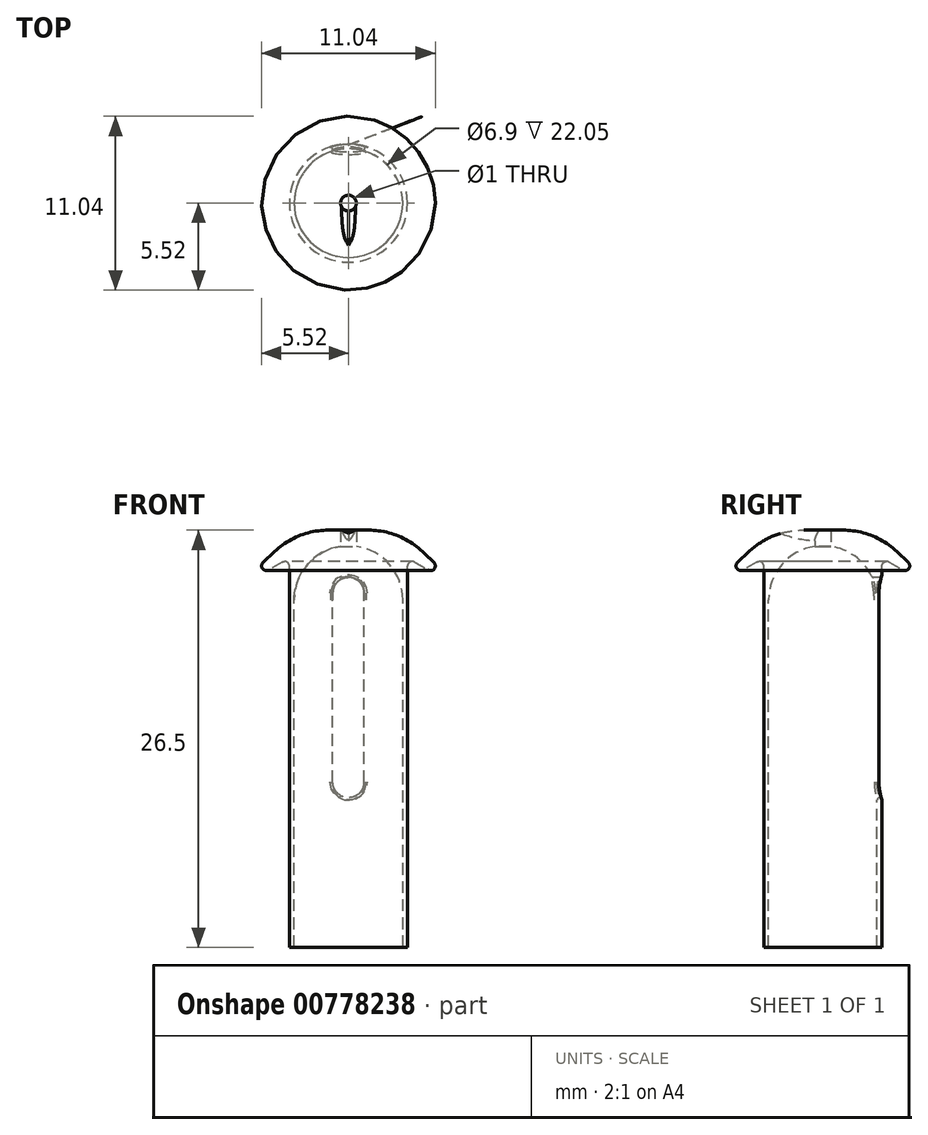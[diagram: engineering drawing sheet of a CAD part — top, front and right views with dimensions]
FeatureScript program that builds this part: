
annotation { "Feature Type Name" : "Feature", "Feature Type Description" : "" }
export const myFeature = defineFeature(function(context is Context, id is Id, definition is map)
    precondition{}
    {
        {
            var Q0;
            Q0=qCreatedBy(makeId("Front.planeOp"),FACE);
            var sketch = newSketch(context, id + "F0", { "sketchPlane" : qUnion([Q0])});
            skLineSegment(sketch, "E0", {"start": v(0, 10.59) * mm, "end": v(0, -11.76) * mm, "construction": true});
            skCircle(sketch, "E1", {"center": v(0, 0) * mm, "radius": 8.5 * mm, "construction": true});
            skCircle(sketch, "E2.0", {"center": v(0, 0) * mm, "radius": 8.2 * mm, "construction": true});
            skLineSegment(sketch, "E3", {"start": v(-3.25, 10) * mm, "end": v(0, 10) * mm});
            skLineSegment(sketch, "E4", {"start": v(-3.45, 0) * mm, "end": v(-3.45, 5.55) * mm});
            skArc(sketch, "E5", {"start": v(0, 9) * mm, "mid": v(-2.44, 7.99) * mm, "end": v(-3.45, 5.55) * mm});
            skLineSegment(sketch, "E6", {"start": v(-3.75, 7.7) * mm, "end": v(-3.75, 0) * mm});
            skLineSegment(sketch, "E7", {"start": v(-4.2, 7.97) * mm, "end": v(-5.07, 7.47) * mm});
            skArc(sketch, "E8", {"start": v(-5.42, 7.95) * mm, "mid": v(-5.46, 7.55) * mm, "end": v(-5.07, 7.47) * mm});
            skArc(sketch, "E9", {"start": v(-3.75, 7.7) * mm, "mid": v(-3.9, 7.97) * mm, "end": v(-4.2, 7.97) * mm});
            skLineSegment(sketch, "E10", {"start": v(-3.75, 0) * mm, "end": v(-3.75, -16.5) * mm});
            skLineSegment(sketch, "E11", {"start": v(-3.45, 0) * mm, "end": v(-3.45, -16.5) * mm});
            skLineSegment(sketch, "E12", {"start": v(-3.45, -16.5) * mm, "end": v(-3.75, -16.5) * mm});
            skLineSegment(sketch, "E13", {"start": v(-5.42, 7.95) * mm, "end": v(-3.25, 10) * mm});
            skLineSegment(sketch, "E14", {"start": v(0, 10) * mm, "end": v(0, 9) * mm});
            skSolve(sketch);
        }
        {
            var Q0;
            Q0 = qSketchRegion(id + "F0", true);
            var Q1;
            Q1=sQuery(id+"F0.wireOp",EDGE,"E0");
            revolve(context, id + "F1", {"surfaceOperationType" : NewSurfaceOperationType.NEW, "entities" : qUnion([Q0]), "axis" : qUnion([Q1]), "revolveType" : RevolveType.FULL});
        }
        {
            var Q0;
            Q0=qCreatedBy(makeId("Right.planeOp"),FACE);
            var sketch = newSketch(context, id + "F2", { "sketchPlane" : qUnion([Q0])});
            skLineSegment(sketch, "E15", {"start": v(0, 16.27) * mm, "end": v(0, 11.43) * mm, "construction": true});
            skArc(sketch, "E16", {"start": v(-6.03, 12.15) * mm, "mid": v(-3.33, 10.06) * mm, "end": v(0, 9.3) * mm});
            skSolve(sketch);
        }
        {
            var Q0;
            Q0=sQuery(id+"F2.wireOp",EDGE,"E16");
            var Q1;
            Q1=sQuery(id+"F2.wireOp",VERTEX,"E16.start");
            cPlane(context, id + "F3", {"entities" : qUnion([Q0, Q1]), "cplaneType" : CPlaneType.CURVE_POINT, "offset" : 25 * mm, "width" : 150 * mm, "height" : 150 * mm});
        }
        {
            var Q0;
            Q0=qCreatedBy(id+"F3.planeOp",FACE);
            var sketch = newSketch(context, id + "F4", { "sketchPlane" : qUnion([Q0])});
            skLineSegment(sketch, "E17", {"start": v(0.5, -4.1) * mm, "end": v(0, -4.1) * mm});
            skLineSegment(sketch, "E18", {"start": v(0, -5.51) * mm, "end": v(0, -3.91) * mm, "construction": true});
            skArc(sketch, "E19", {"start": v(0.5, -4.1) * mm, "mid": v(0.35, -3.56) * mm, "end": v(0, -3.1) * mm});
            skLineSegment(sketch, "E20.MirrorCS", {"start": v(-0.5, -4.1) * mm, "end": v(0, -4.1) * mm});
            skArc(sketch, "E21.MirrorCS", {"start": v(-0.5, -4.1) * mm, "mid": v(-0.35, -3.56) * mm, "end": v(0, -3.1) * mm});
            skSolve(sketch);
        }
        {
            var Q0;
            Q0=makeQuery(id+"F4.imprint","IMPRINT",FACE,{"disambiguationData":[TD([[makeQuery(id+"F4.imprint","IMPRINT",EDGE,{"derivedFrom":sQuery(id+"F4.wireOp",EDGE,"E17")}),-1.0]])]});
            var Q1;
            Q1 = qConstructionFilter(qBodyType(qCreatedBy(id + "F2" ,EDGE), BodyType.WIRE), ConstructionObject.NO);
            sweep(context, id + "F5", {"operationType" : NewBodyOperationType.REMOVE, "profiles" : qUnion([Q0]), "path" : qUnion([Q1])});
        }
        {
            var Q0;
            Q0=qCreatedBy(makeId("Top.planeOp"),FACE);
            var sketch = newSketch(context, id + "F6", { "sketchPlane" : qUnion([Q0])});
            skCircle(sketch, "E22", {"center": v(0, 0) * mm, "radius": 0.5 * mm});
            skSolve(sketch);
        }
        {
            var Q0;
            Q0 = qSketchRegion(id + "F6", true);
            extrude(context, id + "F7", {"entities" : qUnion([Q0]), "operationType" : NewBodyOperationType.REMOVE, "endBound" : BoundingType.THROUGH_ALL, "depth" : 25 * mm, "offsetDistance" : 25 * mm});
        }
        {
            var Q0;
            Q0=qCreatedBy(makeId("Front.planeOp"),FACE);
            var sketch = newSketch(context, id + "F8", { "sketchPlane" : qUnion([Q0])});
            skLineSegment(sketch, "E23", {"start": v(0, 6) * mm, "end": v(0, -6) * mm, "construction": true});
            skArc(sketch, "E24", {"start": v(1, 6) * mm, "mid": v(0, 7) * mm, "end": v(-1, 6) * mm});
            skArc(sketch, "E25", {"start": v(-1, -6) * mm, "mid": v(0, -7) * mm, "end": v(1, -6) * mm});
            skLineSegment(sketch, "E26", {"start": v(-1, 6) * mm, "end": v(-1, -6) * mm});
            skLineSegment(sketch, "E27", {"start": v(1, 6) * mm, "end": v(1, -6) * mm});
            skSolve(sketch);
        }
        {
            var Q0;
            Q0 = qSketchRegion(id + "F8", true);
            extrude(context, id + "F9", {"entities" : qUnion([Q0]), "operationType" : NewBodyOperationType.REMOVE, "endBound" : BoundingType.THROUGH_ALL, "oppositeDirection" : true, "depth" : 25 * mm, "offsetDistance" : 25 * mm});
        }
        {
            var Q0;
            Q0=makeQuery(id+"F9.boolean.opBoolean","COPY",FACE,{"derivedFrom":makeQuery(id+"F9.opExtrude","SWEPT_FACE",FACE,{"disambiguationData":[OSD([sQuery(id+"F8.wireOp",EDGE,"E24")])]})});
            fillet(context, id + "F10", {"entities" : qUnion([Q0]), "radius" : 0.15 * mm, "tangentPropagation" : true, "allowEdgeOverflow" : false});
        }
        {
            var Q0;
            Q0=makeQuery(id+"F1.opRevolve","SWEPT_EDGE",EDGE,{"disambiguationData":[OSD([sQuery(id+"F0.wireOp",EDGE,"E3"),sQuery(id+"F0.wireOp",EDGE,"E13")])]});
            fillet(context, id + "F11", {"entities" : qUnion([Q0]), "radius" : 5 * mm, "tangentPropagation" : true, "allowEdgeOverflow" : false});
        }
    });
